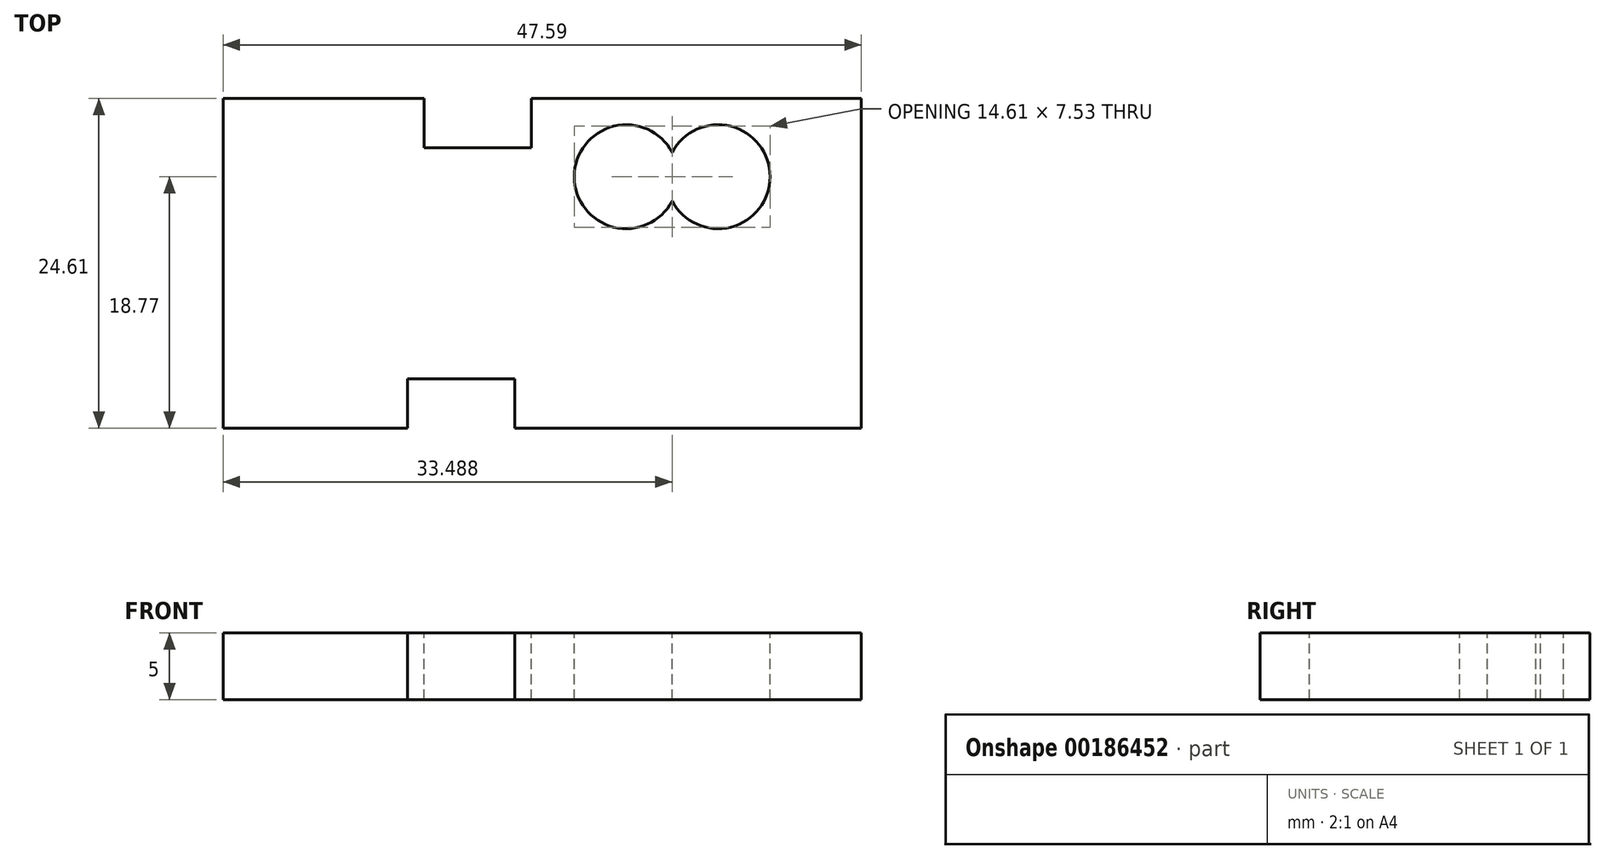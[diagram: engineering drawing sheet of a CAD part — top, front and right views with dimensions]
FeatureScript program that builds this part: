
annotation { "Feature Type Name" : "Feature", "Feature Type Description" : "" }
export const myFeature = defineFeature(function(context is Context, id is Id, definition is map)
    precondition{}
    {
        {
            var Q0;
            Q0=qCreatedBy(makeId("Top.planeOp"),FACE);
            var sketch = newSketch(context, id + "F0", { "sketchPlane" : qUnion([Q0])});
            skLineSegment(sketch, "E0.bottom", {"start": v(-18.7, 16.71) * mm, "end": v(-3.73, 16.71) * mm});
            skLineSegment(sketch, "E0.left", {"start": v(-18.7, 16.71) * mm, "end": v(-18.7, -7.9) * mm});
            skLineSegment(sketch, "E0.right", {"start": v(28.89, 16.71) * mm, "end": v(28.89, -7.9) * mm});
            skLineSegment(sketch, "E1", {"start": v(-3.73, 16.71) * mm, "end": v(-3.73, 13.02) * mm});
            skLineSegment(sketch, "E2", {"start": v(-3.73, 13.02) * mm, "end": v(4.27, 13.02) * mm});
            skLineSegment(sketch, "E3", {"start": v(4.27, 13.02) * mm, "end": v(4.27, 16.71) * mm});
            skLineSegment(sketch, "E4.trimOffspring", {"start": v(4.27, 16.71) * mm, "end": v(28.89, 16.71) * mm});
            skLineSegment(sketch, "E5", {"start": v(-18.7, -7.9) * mm, "end": v(-4.96, -7.9) * mm});
            skLineSegment(sketch, "E6", {"start": v(-4.96, -7.9) * mm, "end": v(-4.96, -4.2) * mm});
            skLineSegment(sketch, "E7", {"start": v(-4.96, -4.2) * mm, "end": v(3.04, -4.2) * mm});
            skLineSegment(sketch, "E8", {"start": v(3.04, -4.2) * mm, "end": v(3.04, -7.9) * mm});
            skLineSegment(sketch, "E9.trimOffspring", {"start": v(3.04, -7.9) * mm, "end": v(28.89, -7.9) * mm});
            skArc(sketch, "E10", {"start": v(14.79, 12.68) * mm, "mid": v(7.48, 10.87) * mm, "end": v(14.79, 9.06) * mm});
            skArc(sketch, "E11", {"start": v(14.79, 9.06) * mm, "mid": v(22.1, 10.87) * mm, "end": v(14.79, 12.68) * mm});
            skSolve(sketch);
        }
        {
            var Q0;
            Q0=makeQuery(id+"F0.imprint","IMPRINT",FACE,{"disambiguationData":[TD([[makeQuery(id+"F0.imprint","IMPRINT",EDGE,{"derivedFrom":sQuery(id+"F0.wireOp",EDGE,"E0.bottom")}),-1.0]])]});
            extrude(context, id + "F1", {"entities" : qUnion([Q0]), "oppositeDirection" : true, "depth" : 5 * mm});
        }
    });
